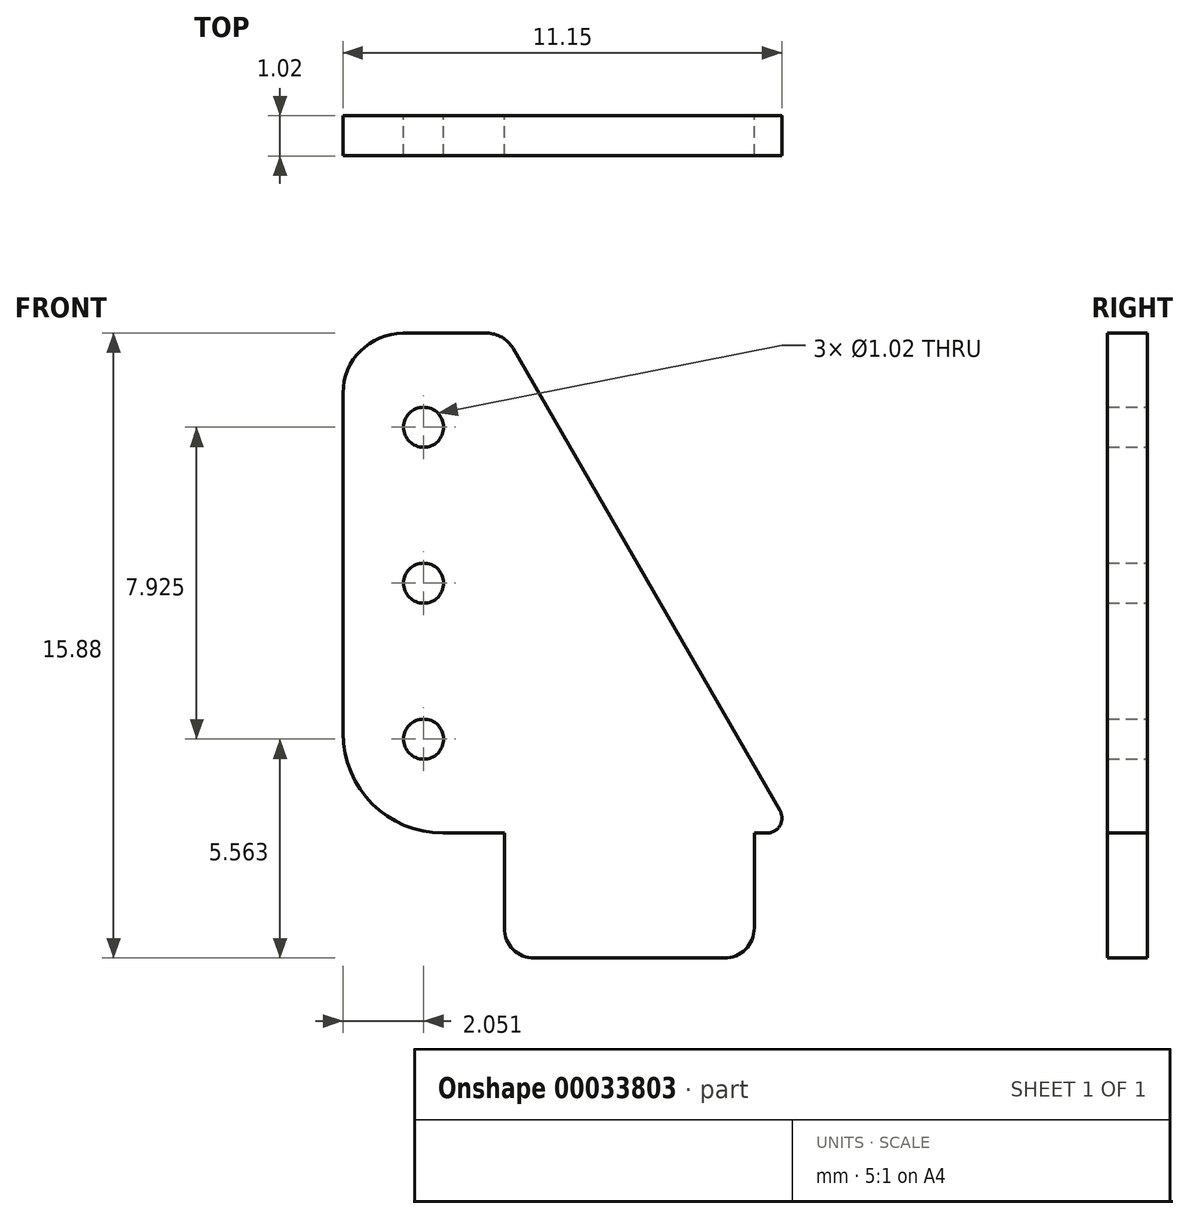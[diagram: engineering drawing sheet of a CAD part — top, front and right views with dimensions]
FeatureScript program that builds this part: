
annotation { "Feature Type Name" : "Feature", "Feature Type Description" : "" }
export const myFeature = defineFeature(function(context is Context, id is Id, definition is map)
    precondition{}
    {
        {
            var Q0;
            Q0=qCreatedBy(makeId("Front.planeOp"),FACE);
            var sketch = newSketch(context, id + "F0", { "sketchPlane" : qUnion([Q0])});
            skLineSegment(sketch, "E0", {"start": v(0, 0.76) * mm, "end": v(0, 3.17) * mm});
            skLineSegment(sketch, "E1", {"start": v(0.76, 0) * mm, "end": v(5.59, 0) * mm});
            skLineSegment(sketch, "E2", {"start": v(6.35, 0.76) * mm, "end": v(6.35, 3.18) * mm});
            skLineSegment(sketch, "E3", {"start": v(6.35, 3.18) * mm, "end": v(6.67, 3.18) * mm});
            skLineSegment(sketch, "E4", {"start": v(7, 3.75) * mm, "end": v(0.22, 15.5) * mm});
            skLineSegment(sketch, "E5", {"start": v(-0.44, 15.88) * mm, "end": v(-2.57, 15.88) * mm});
            skLineSegment(sketch, "E6", {"start": v(-4.1, 14.35) * mm, "end": v(-4.1, 5.72) * mm});
            skLineSegment(sketch, "E7", {"start": v(0, 3.18) * mm, "end": v(-1.56, 3.18) * mm});
            skLineSegment(sketch, "E8", {"start": v(-2.05, 3.18) * mm, "end": v(-2.05, 15.88) * mm, "construction": true});
            skCircle(sketch, "E9", {"center": v(-2.05, 9.53) * mm, "radius": 0.5 * mm});
            skCircle(sketch, "E10", {"center": v(-2.05, 5.56) * mm, "radius": 0.5 * mm});
            skCircle(sketch, "E11", {"center": v(-2.05, 13.49) * mm, "radius": 0.5 * mm});
            skPoint(sketch, "E12.perimeterSnap0", {"position": v(0, 1.59) * mm});
            skPoint(sketch, "E13.visualSharp", {"position": v(-4.1, 3.18) * mm});
            skArc(sketch, "E13.filletArc", {"start": v(-4.1, 5.72) * mm, "mid": v(-3.35, 3.92) * mm, "end": v(-1.56, 3.18) * mm});
            skPoint(sketch, "E14.visualSharp", {"position": v(-4.1, 15.88) * mm});
            skArc(sketch, "E14.filletArc", {"start": v(-2.57, 15.88) * mm, "mid": v(-3.65, 15.43) * mm, "end": v(-4.1, 14.35) * mm});
            skPoint(sketch, "E15.visualSharp", {"position": v(0, 15.88) * mm});
            skArc(sketch, "E15.filletArc", {"start": v(0.22, 15.5) * mm, "mid": v(-0.06, 15.77) * mm, "end": v(-0.44, 15.88) * mm});
            skPoint(sketch, "E16.visualSharp", {"position": v(7.33, 3.18) * mm});
            skArc(sketch, "E16.filletArc", {"start": v(6.67, 3.17) * mm, "mid": v(7, 3.37) * mm, "end": v(7, 3.75) * mm});
            skPoint(sketch, "E17.visualSharp", {"position": v(6.35, 0) * mm});
            skArc(sketch, "E17.filletArc", {"start": v(5.59, 0) * mm, "mid": v(6.13, 0.22) * mm, "end": v(6.35, 0.76) * mm});
            skPoint(sketch, "E18.visualSharp", {"position": v(0, 0) * mm});
            skArc(sketch, "E18.filletArc", {"start": v(0, 0.76) * mm, "mid": v(0.22, 0.22) * mm, "end": v(0.76, 0) * mm});
            skSolve(sketch);
        }
        {
            var Q0;
            Q0 = qSketchRegion(id + "F0", true);
            extrude(context, id + "F1", {"entities" : qUnion([Q0]), "depth" : 1.02 * mm});
        }
    });
